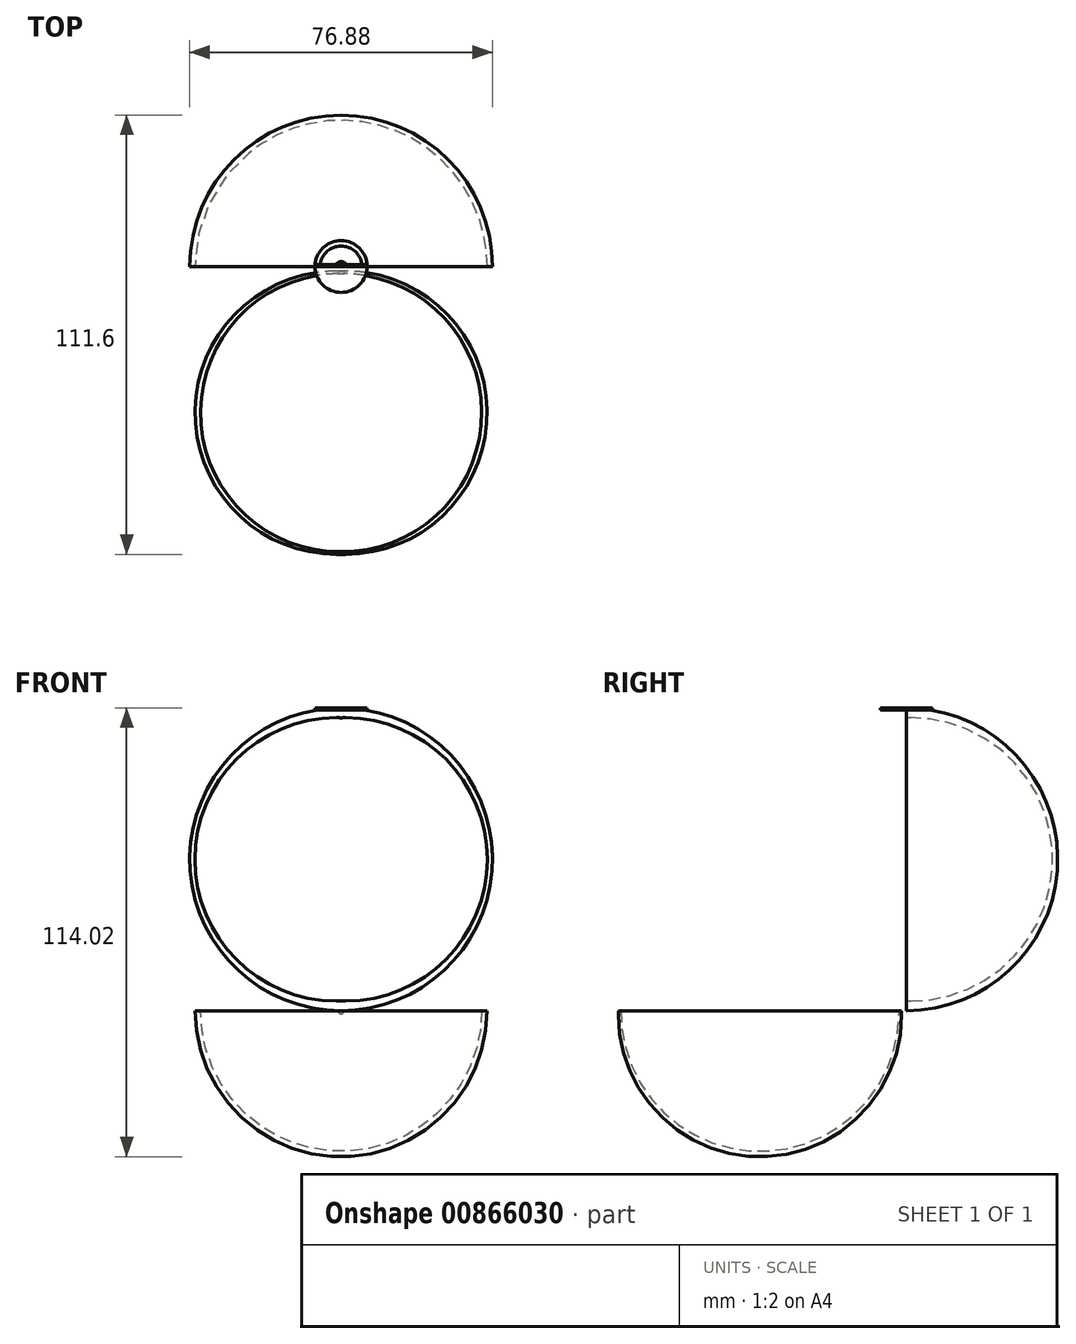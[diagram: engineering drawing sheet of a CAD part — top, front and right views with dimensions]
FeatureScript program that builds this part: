
annotation { "Feature Type Name" : "Feature", "Feature Type Description" : "" }
export const myFeature = defineFeature(function(context is Context, id is Id, definition is map)
    precondition{}
    {
        {
            var Q0;
            Q0=qCreatedBy(makeId("Front.planeOp"),FACE);
            var sketch = newSketch(context, id + "F0", { "sketchPlane" : qUnion([Q0])});
            skArc(sketch, "E0", {"start": v(0, 0) * mm, "mid": v(38.44, 38.44) * mm, "end": v(0, 76.88) * mm});
            skLineSegment(sketch, "E1", {"start": v(0, 76.88) * mm, "end": v(0, 74.42) * mm});
            skLineSegment(sketch, "E2", {"start": v(0, 0) * mm, "end": v(0, 2.47) * mm});
            skArc(sketch, "E3", {"start": v(0, 2.47) * mm, "mid": v(37.14, 38.44) * mm, "end": v(0, 74.42) * mm});
            skLineSegment(sketch, "E4", {"start": v(0, 76.88) * mm, "end": v(6.47, 76.88) * mm});
            skLineSegment(sketch, "E5", {"start": v(6.47, 76.88) * mm, "end": v(-6.45, 76.88) * mm});
            skLineSegment(sketch, "E6", {"start": v(6.47, 76.88) * mm, "end": v(6.47, 76.93) * mm});
            skLineSegment(sketch, "E7", {"start": v(6.47, 76.93) * mm, "end": v(-6.45, 76.93) * mm});
            skLineSegment(sketch, "E8", {"start": v(-6.45, 76.93) * mm, "end": v(-6.45, 76.88) * mm});
            skSolve(sketch);
        }
        {
            var Q0;
            Q0=makeQuery(id+"F0.imprint","IMPRINT",FACE,{"disambiguationData":[TD([[makeQuery(id+"F0.imprint","IMPRINT",EDGE,{"derivedFrom":sQuery(id+"F0.wireOp",EDGE,"E0")}),1.0]])]});
            var Q1;
            Q1=sQuery(id+"F0.wireOp",EDGE,"E1");
            revolve(context, id + "F1", {"surfaceOperationType" : NewSurfaceOperationType.NEW, "entities" : qUnion([Q0]), "axis" : qUnion([Q1]), "revolveType" : RevolveType.ONE_DIRECTION, "oppositeDirection" : true, "angle" : 180 * degree});
        }
        {
            var Q0;
            {var subQ0=sQuery(id+"F0.wireOp",EDGE,"E6");Q0=makeQuery(id+"F0.imprint","IMPRINT",FACE,{"disambiguationData":[TD([[makeQuery(id+"F0.imprint","IMPRINT",EDGE,{"derivedFrom":subQ0}),1.0]])]});}
            extrude(context, id + "F2", {"entities" : qUnion([Q0]), "oppositeDirection" : true, "depth" : 0.5 * mm, "offsetDistance" : 25.4 * mm});
        }
        {
            var Q0;
            Q0=makeQuery(id+"F2.opExtrude","SWEPT_FACE",FACE,{"disambiguationData":[OSD([sQuery(id+"F0.wireOp",EDGE,"E7")])]});
            var sketch = newSketch(context, id + "F3", { "sketchPlane" : qUnion([Q0])});
            skCircle(sketch, "E9", {"center": v(0, 0) * mm, "radius": 6.6 * mm});
            skLineSegment(sketch, "E10", {"start": v(-5.3, 0.5) * mm, "end": v(5.34, 0.5) * mm});
            skArc(sketch, "E11", {"start": v(5.34, 0.5) * mm, "mid": v(0.02, 5.18) * mm, "end": v(-5.3, 0.5) * mm});
            skCircle(sketch, "E12", {"center": v(0.02, -0.18) * mm, "radius": 1.43 * mm});
            skLineSegment(sketch, "E13", {"start": v(-5.3, 0.5) * mm, "end": v(-5.3, 0) * mm});
            skLineSegment(sketch, "E14", {"start": v(-5.3, 0) * mm, "end": v(-1.4, 0) * mm});
            skLineSegment(sketch, "E15", {"start": v(5.34, 0.5) * mm, "end": v(5.4, 0) * mm});
            skLineSegment(sketch, "E16", {"start": v(5.4, 0) * mm, "end": v(1.44, 0) * mm});
            skLineSegment(sketch, "E17", {"start": v(6.6, 0) * mm, "end": v(-6.6, 0) * mm});
            skSolve(sketch);
        }
        {
            var Q0;
            {var subQ7=sQuery(id+"F3.wireOp",EDGE,"E11");Q0=makeQuery(id+"F3.imprint","IMPRINT",FACE,{"disambiguationData":[TD([[makeQuery(id+"F3.imprint","IMPRINT",EDGE,{"derivedFrom":subQ7}),-1.0]])]});}
            var Q1;
            {var subQ0=sQuery(id+"F3.wireOp",EDGE,"E17");var subQ4=sQuery(id+"F3.wireOp",EDGE,"E9");var subQ5=makeQuery(id+"F3.imprint","INTERSECT",VERTEX,{"disambiguationData":[OD(0.0)],"derivedFrom":[subQ4,subQ0]});Q1=makeQuery(id+"F3.imprint","IMPRINT",FACE,{"disambiguationData":[TD([[makeQuery(id+"F3.imprint","IMPRINT",EDGE,{"disambiguationData":[TD([[subQ5,1.0]])],"derivedFrom":subQ4}),1.0]])]});}
            var Q2;
            {var subQ0=sQuery(id+"F3.wireOp",EDGE,"E17");var subQ1=sQuery(id+"F3.wireOp",EDGE,"E12");var subQ2=makeQuery(id+"F3.imprint","INTERSECT",VERTEX,{"disambiguationData":[OD(0.0)],"derivedFrom":[subQ1,subQ0]});Q2=makeQuery(id+"F3.imprint","IMPRINT",FACE,{"disambiguationData":[TD([[makeQuery(id+"F3.imprint","IMPRINT",EDGE,{"disambiguationData":[TD([[subQ2,1.0]])],"derivedFrom":subQ1}),1.0]])]});}
            var Q3;
            {var subQ0=sQuery(id+"F3.wireOp",EDGE,"E12");var subQ1=sQuery(id+"F3.wireOp",EDGE,"E10");var subQ2=makeQuery(id+"F3.imprint","INTERSECT",VERTEX,{"disambiguationData":[OD(0.0)],"derivedFrom":[subQ1,subQ0]});Q3=makeQuery(id+"F3.imprint","IMPRINT",FACE,{"disambiguationData":[TD([[makeQuery(id+"F3.imprint","IMPRINT",EDGE,{"disambiguationData":[TD([[subQ2,-1.0]])],"derivedFrom":subQ1}),1.0]])]});}
            var Q4;
            {var subQ0=sQuery(id+"F3.wireOp",EDGE,"E12");var subQ1=sQuery(id+"F3.wireOp",EDGE,"E10");var subQ2=makeQuery(id+"F3.imprint","INTERSECT",VERTEX,{"disambiguationData":[OD(0.0)],"derivedFrom":[subQ1,subQ0]});Q4=makeQuery(id+"F3.imprint","IMPRINT",FACE,{"disambiguationData":[TD([[makeQuery(id+"F3.imprint","IMPRINT",EDGE,{"disambiguationData":[TD([[subQ2,-1.0]])],"derivedFrom":subQ1}),-1.0]])]});}
            var Q5;
            {var subQ0=sQuery(id+"F3.wireOp",EDGE,"E13");Q5=makeQuery(id+"F3.imprint","IMPRINT",FACE,{"disambiguationData":[TD([[makeQuery(id+"F3.imprint","IMPRINT",EDGE,{"derivedFrom":subQ0}),-1.0]])]});}
            var Q6;
            {var subQ0=sQuery(id+"F3.wireOp",EDGE,"E15");Q6=makeQuery(id+"F3.imprint","IMPRINT",FACE,{"disambiguationData":[TD([[makeQuery(id+"F3.imprint","IMPRINT",EDGE,{"derivedFrom":subQ0}),1.0]])]});}
            extrude(context, id + "F4", {"entities" : qUnion([Q0, Q1, Q2, Q3, Q4, Q5, Q6]), "oppositeDirection" : true, "depth" : 0.5 * mm, "offsetDistance" : 25.4 * mm});
        }
        {
            var Q0;
            {var subQ0=sQuery(id+"F3.wireOp",EDGE,"E11");Q0=makeQuery(id+"F3.imprint","IMPRINT",FACE,{"disambiguationData":[TD([[makeQuery(id+"F3.imprint","IMPRINT",EDGE,{"derivedFrom":subQ0}),1.0]])]});}
            var Q1;
            {var subQ0=sQuery(id+"F3.wireOp",EDGE,"E13");Q1=makeQuery(id+"F3.imprint","IMPRINT",FACE,{"disambiguationData":[TD([[makeQuery(id+"F3.imprint","IMPRINT",EDGE,{"derivedFrom":subQ0}),1.0]])]});}
            var Q2;
            {var subQ0=sQuery(id+"F3.wireOp",EDGE,"E15");Q2=makeQuery(id+"F3.imprint","IMPRINT",FACE,{"disambiguationData":[TD([[makeQuery(id+"F3.imprint","IMPRINT",EDGE,{"derivedFrom":subQ0}),-1.0]])]});}
            extrude(context, id + "F5", {"entities" : qUnion([Q0, Q1, Q2]), "oppositeDirection" : true, "depth" : 0.25 * mm, "offsetDistance" : 25.4 * mm});
        }
        {
            var Q0;
            Q0=qCreatedBy(makeId("Right.planeOp"),FACE);
            var sketch = newSketch(context, id + "F6", { "sketchPlane" : qUnion([Q0])});
            skArc(sketch, "E18", {"start": v(-73.14, 0) * mm, "mid": v(-37.56, -37.09) * mm, "end": v(-1.19, -0.78) * mm});
            skLineSegment(sketch, "E19", {"start": v(-1.19, -0.78) * mm, "end": v(-1.84, -0.78) * mm});
            skArc(sketch, "E20", {"start": v(-72.49, 0) * mm, "mid": v(-37.55, -35.71) * mm, "end": v(-1.84, -0.78) * mm});
            skLineSegment(sketch, "E21", {"start": v(-73.14, 0) * mm, "end": v(-72.49, 0) * mm});
            skSolve(sketch);
        }
        {
            var Q0;
            Q0 = qSketchRegion(id + "F6", true);
            var Q1;
            Q1=sQuery(id+"F6.wireOp",EDGE,"E21");
            revolve(context, id + "F7", {"surfaceOperationType" : NewSurfaceOperationType.NEW, "entities" : qUnion([Q0]), "axis" : qUnion([Q1]), "revolveType" : RevolveType.SYMMETRIC, "angle" : 180 * degree});
        }
    });
